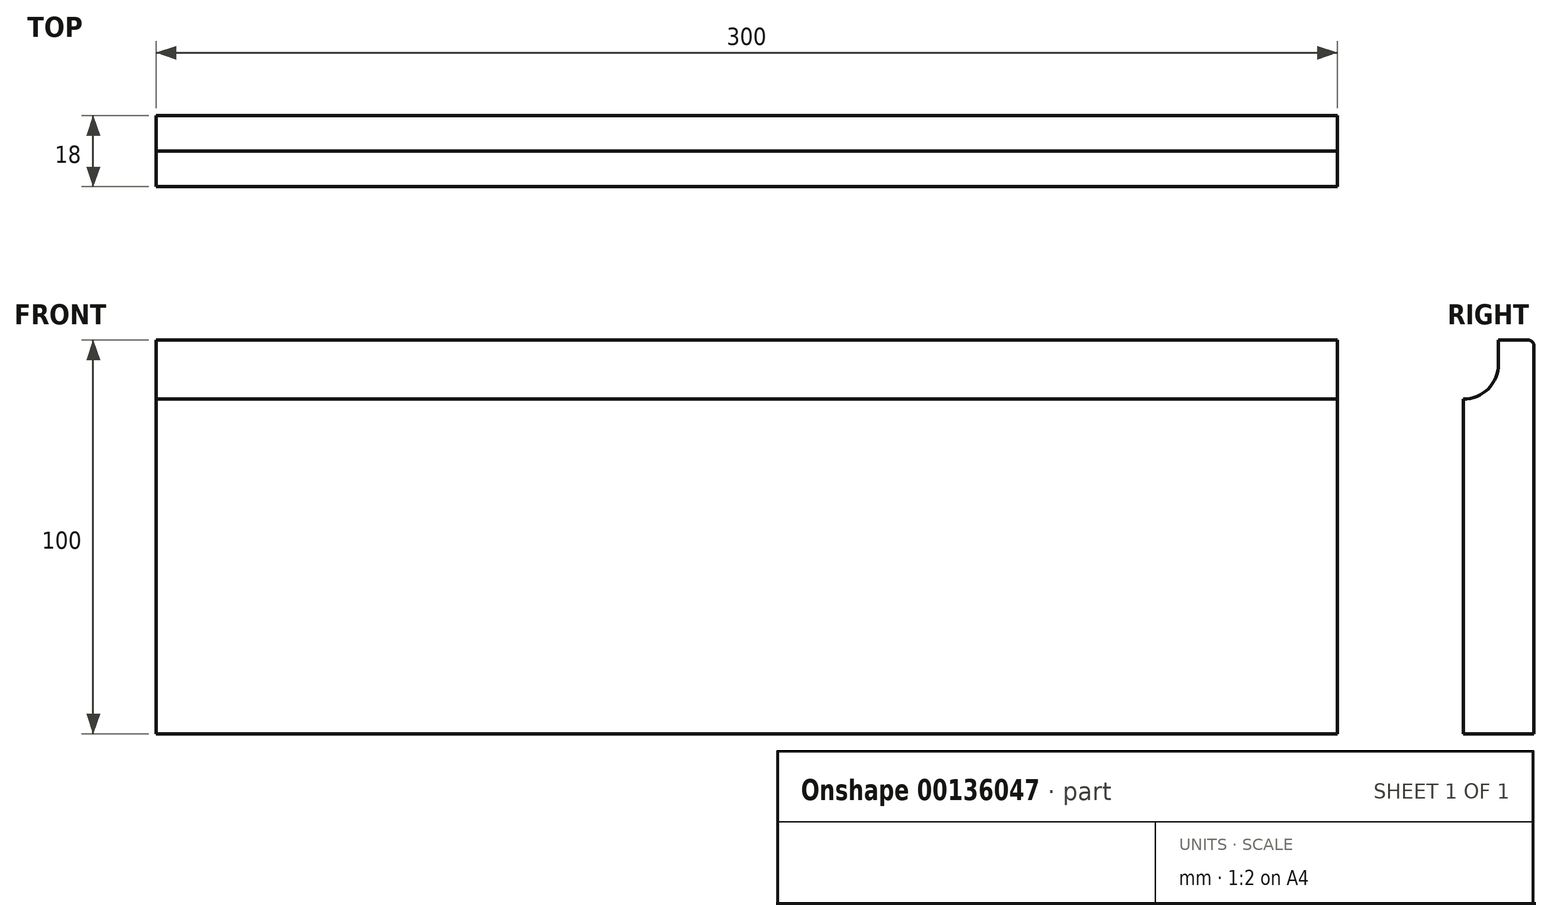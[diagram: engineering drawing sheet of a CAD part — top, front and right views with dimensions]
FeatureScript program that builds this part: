
annotation { "Feature Type Name" : "Feature", "Feature Type Description" : "" }
export const myFeature = defineFeature(function(context is Context, id is Id, definition is map)
    precondition{}
    {
        {
            var Q0;
            Q0=qCreatedBy(makeId("Front.planeOp"),FACE);
            var sketch = newSketch(context, id + "F0", { "sketchPlane" : qUnion([Q0])});
            skLineSegment(sketch, "E0.bottom", {"start": v(-153.72, -55.78) * mm, "end": v(146.28, -55.78) * mm});
            skLineSegment(sketch, "E0.top", {"start": v(-153.72, -155.78) * mm, "end": v(146.28, -155.78) * mm});
            skLineSegment(sketch, "E0.left", {"start": v(-153.72, -55.78) * mm, "end": v(-153.72, -155.78) * mm});
            skLineSegment(sketch, "E0.right", {"start": v(146.28, -55.78) * mm, "end": v(146.28, -155.78) * mm});
            skSolve(sketch);
        }
        {
            var Q0;
            Q0=makeQuery(id+"F0.imprint","IMPRINT",FACE,{"disambiguationData":[TD([[makeQuery(id+"F0.imprint","IMPRINT",EDGE,{"derivedFrom":sQuery(id+"F0.wireOp",EDGE,"E0.bottom")}),-1.0]])]});
            extrude(context, id + "F1", {"entities" : qUnion([Q0]), "endBound" : BoundingType.SYMMETRIC, "depth" : 18 * mm});
        }
        {
            var Q0;
            Q0=makeQuery(id+"F1.opExtrude","SWEPT_FACE",FACE,{"disambiguationData":[OSD([sQuery(id+"F0.wireOp",EDGE,"E0.right")])]});
            var sketch = newSketch(context, id + "F2", { "sketchPlane" : qUnion([Q0])});
            skLineSegment(sketch, "E1", {"start": v(0, -55.78) * mm, "end": v(0, -61.78) * mm});
            skLineSegment(sketch, "E2", {"start": v(-9, -70.78) * mm, "end": v(-9, -70.78) * mm});
            skLineSegment(sketch, "E3", {"start": v(-9, -70.78) * mm, "end": v(-9, -55.78) * mm});
            skLineSegment(sketch, "E4", {"start": v(-9, -55.78) * mm, "end": v(0, -55.78) * mm});
            skPoint(sketch, "E5.visualSharp", {"position": v(0, -70.78) * mm});
            skArc(sketch, "E5.filletArc", {"start": v(-9, -70.78) * mm, "mid": v(-2.64, -68.14) * mm, "end": v(0, -61.78) * mm});
            skSolve(sketch);
        }
        {
            var Q0;
            Q0=makeQuery(id+"F2.imprint","IMPRINT",FACE,{"disambiguationData":[TD([[makeQuery(id+"F2.imprint","IMPRINT",EDGE,{"derivedFrom":sQuery(id+"F2.wireOp",EDGE,"E1")}),-1.0]])]});
            extrude(context, id + "F3", {"entities" : qUnion([Q0]), "operationType" : NewBodyOperationType.REMOVE, "endBound" : BoundingType.THROUGH_ALL, "oppositeDirection" : true, "depth" : 25 * mm});
        }
        {
            var Q0;
            Q0=makeQuery(id+"F1.opExtrude","CAP_EDGE",EDGE,{"disambiguationData":[OSD([sQuery(id+"F0.wireOp",EDGE,"E0.bottom")])],"isStart":false});
            var Q1;
            Q1=makeQuery(id+"F3.boolean.opBoolean","COPY",EDGE,{"derivedFrom":makeQuery(id+"F3.opExtrude","SWEPT_EDGE",EDGE,{"disambiguationData":[OSD([sQuery(id+"F0.wireOp",EDGE,"E0.bottom"),sQuery(id+"F0.wireOp",EDGE,"E0.right"),sQuery(id+"F2.wireOp",EDGE,"E3"),sQuery(id+"F2.wireOp",EDGE,"E4")])]})});
            var Q2;
            Q2=makeQuery(id+"F3.boolean.opBoolean","COPY",EDGE,{"derivedFrom":makeQuery(id+"F3.opExtrude","SWEPT_EDGE",EDGE,{"disambiguationData":[OSD([sQuery(id+"F0.wireOp",EDGE,"E0.bottom"),sQuery(id+"F0.wireOp",EDGE,"E0.right"),sQuery(id+"F2.wireOp",EDGE,"E1"),sQuery(id+"F2.wireOp",EDGE,"E4")])]})});
            var Q3;
            Q3=makeQuery(id+"F1.opExtrude","CAP_EDGE",EDGE,{"disambiguationData":[OSD([sQuery(id+"F0.wireOp",EDGE,"E0.bottom")])],"isStart":true});
            var Q4;
            Q4=makeQuery(id+"F3.boolean.opBoolean","COPY",EDGE,{"derivedFrom":makeQuery(id+"F3.opExtrude","SWEPT_EDGE",EDGE,{"disambiguationData":[OSD([sQuery(id+"F0.wireOp",EDGE,"E0.right"),sQuery(id+"F2.wireOp",EDGE,"E3"),sQuery(id+"F2.wireOp",EDGE,"E5.filletArc")])]})});
            fillet(context, id + "F4", {"entities" : qUnion([Q0, Q1, Q2, Q3, Q4]), "radius" : 1.5 * mm, "tangentPropagation" : true, "allowEdgeOverflow" : false});
        }
    });
